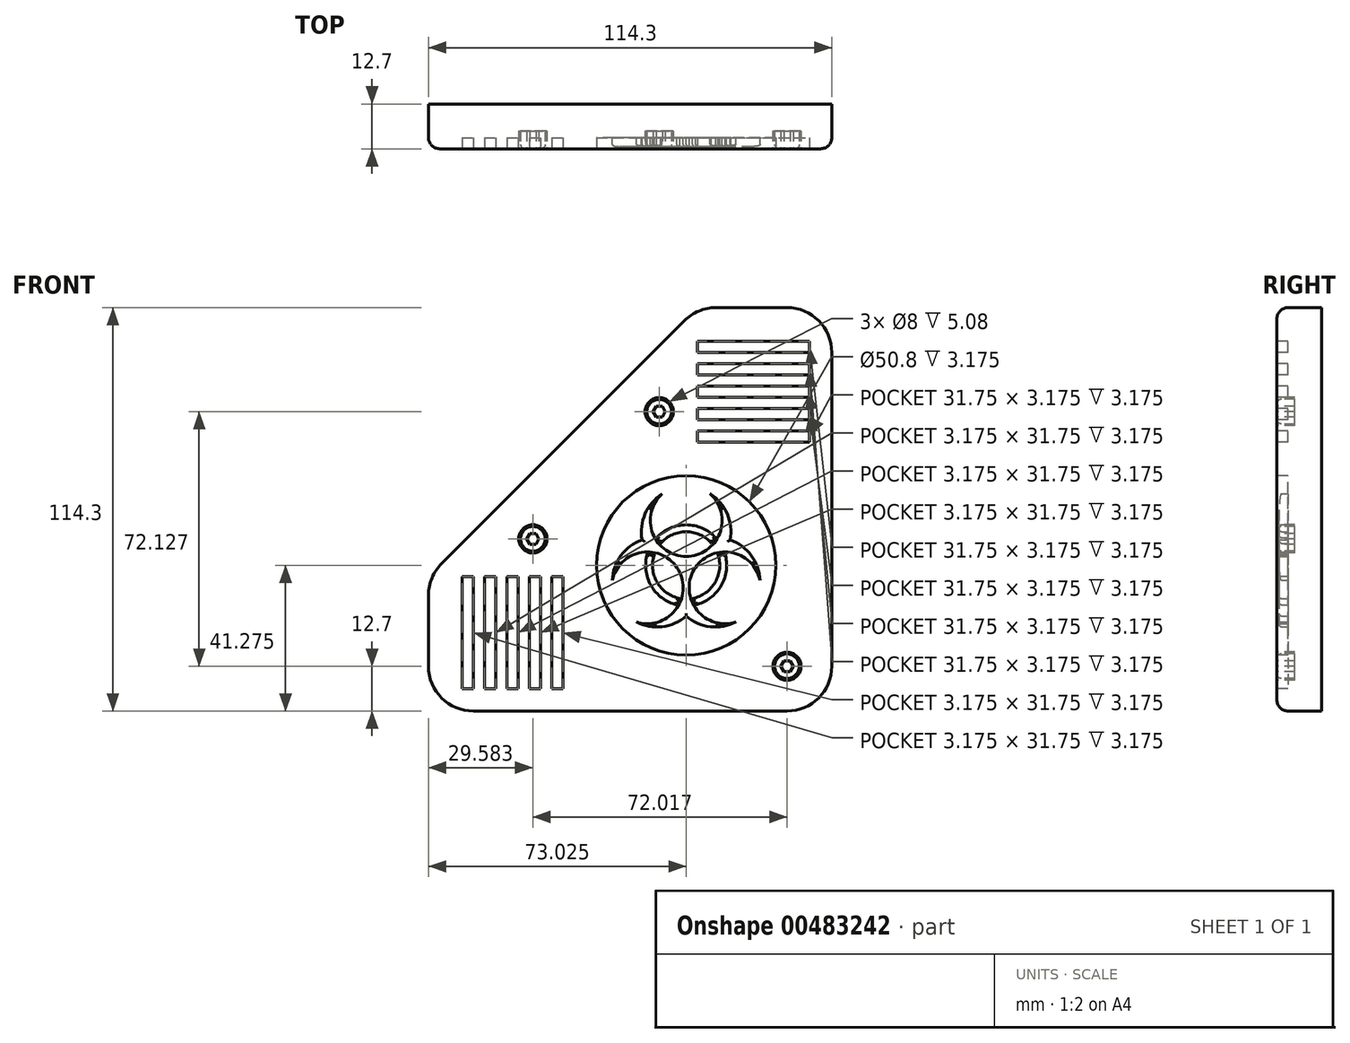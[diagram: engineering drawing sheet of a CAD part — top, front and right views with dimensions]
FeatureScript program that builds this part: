
annotation { "Feature Type Name" : "Feature", "Feature Type Description" : "" }
export const myFeature = defineFeature(function(context is Context, id is Id, definition is map)
    precondition{}
    {
        {
            var Q0;
            Q0=qCreatedBy(makeId("Front.planeOp"),FACE);
            var sketch = newSketch(context, id + "F0", { "sketchPlane" : qUnion([Q0])});
            skLineSegment(sketch, "E0.bottom", {"start": v(63.5, -76.2) * mm, "end": v(-25.4, -76.2) * mm});
            skLineSegment(sketch, "E0.left", {"start": v(76.2, -63.5) * mm, "end": v(76.2, 25.4) * mm});
            skPoint(sketch, "E0.middle", {"position": v(0, 0) * mm});
            skLineSegment(sketch, "E1", {"start": v(-34.38, -34.38) * mm, "end": v(34.38, 34.38) * mm});
            skPoint(sketch, "E0.right.end.orphan", {"position": v(-76.2, 76.2) * mm});
            skPoint(sketch, "E2.visualSharp", {"position": v(76.2, 76.2) * mm});
            skPoint(sketch, "E3.visualSharp", {"position": v(-76.2, -76.2) * mm});
            skPoint(sketch, "E4.visualSharp", {"position": v(76.2, -76.2) * mm});
            skArc(sketch, "E4.filletArc", {"start": v(63.5, -76.2) * mm, "mid": v(72.48, -72.48) * mm, "end": v(76.2, -63.5) * mm});
            skLineSegment(sketch, "E5", {"start": v(63.5, 38.1) * mm, "end": v(43.36, 38.1) * mm});
            skLineSegment(sketch, "E6", {"start": v(-38.1, -43.36) * mm, "end": v(-38.1, -63.5) * mm});
            skPoint(sketch, "E7.visualSharp", {"position": v(38.1, 38.1) * mm});
            skArc(sketch, "E7.filletArc", {"start": v(43.36, 38.1) * mm, "mid": v(38.5, 37.13) * mm, "end": v(34.38, 34.38) * mm});
            skPoint(sketch, "E8.visualSharp", {"position": v(76.2, 38.1) * mm});
            skArc(sketch, "E8.filletArc", {"start": v(76.2, 25.4) * mm, "mid": v(72.48, 34.38) * mm, "end": v(63.5, 38.1) * mm});
            skPoint(sketch, "E9.visualSharp", {"position": v(-38.1, -38.1) * mm});
            skArc(sketch, "E9.filletArc", {"start": v(-34.38, -34.38) * mm, "mid": v(-37.13, -38.5) * mm, "end": v(-38.1, -43.36) * mm});
            skPoint(sketch, "E10.visualSharp", {"position": v(-38.1, -76.2) * mm});
            skArc(sketch, "E10.filletArc", {"start": v(-38.1, -63.5) * mm, "mid": v(-34.38, -72.48) * mm, "end": v(-25.4, -76.2) * mm});
            skSolve(sketch);
        }
        {
            var Q0;
            Q0 = qSketchRegion(id + "F0", true);
            extrude(context, id + "F1", {"entities" : qUnion([Q0]), "depth" : 12.7 * mm});
        }
        {
            var Q0;
            Q0=makeQuery(id+"F1.opExtrude","CAP_FACE",FACE,{"disambiguationData":[OSD([sQuery(id+"F0.wireOp",EDGE,"E0.bottom"),sQuery(id+"F0.wireOp",EDGE,"E0.left"),sQuery(id+"F0.wireOp",EDGE,"E1"),sQuery(id+"F0.wireOp",EDGE,"E4.filletArc"),sQuery(id+"F0.wireOp",EDGE,"E5"),sQuery(id+"F0.wireOp",EDGE,"E6"),sQuery(id+"F0.wireOp",EDGE,"E7.filletArc"),sQuery(id+"F0.wireOp",EDGE,"E8.filletArc"),sQuery(id+"F0.wireOp",EDGE,"E9.filletArc"),sQuery(id+"F0.wireOp",EDGE,"E10.filletArc")])],"isStart":false});
            fillet(context, id + "F2", {"entities" : qUnion([Q0]), "radius" : 3.17 * mm, "tangentPropagation" : true, "allowEdgeOverflow" : false});
        }
        {
            var Q0;
            Q0=makeQuery(id+"F1.opExtrude","CAP_FACE",FACE,{"disambiguationData":[OSD([sQuery(id+"F0.wireOp",EDGE,"E0.bottom"),sQuery(id+"F0.wireOp",EDGE,"E0.left"),sQuery(id+"F0.wireOp",EDGE,"E1"),sQuery(id+"F0.wireOp",EDGE,"E4.filletArc"),sQuery(id+"F0.wireOp",EDGE,"E5"),sQuery(id+"F0.wireOp",EDGE,"E6"),sQuery(id+"F0.wireOp",EDGE,"E7.filletArc"),sQuery(id+"F0.wireOp",EDGE,"E8.filletArc"),sQuery(id+"F0.wireOp",EDGE,"E9.filletArc"),sQuery(id+"F0.wireOp",EDGE,"E10.filletArc")])],"isStart":false});
            var sketch = newSketch(context, id + "F3", { "sketchPlane" : qUnion([Q0])});
            skCircle(sketch, "E11", {"center": v(34.92, -34.92) * mm, "radius": 25.4 * mm});
            skSolve(sketch);
        }
        {
            var Q0;
            Q0 = qSketchRegion(id + "F3", true);
            extrude(context, id + "F4", {"entities" : qUnion([Q0]), "operationType" : NewBodyOperationType.REMOVE, "oppositeDirection" : true, "depth" : 3.17 * mm});
        }
        {
            var Q0;
            Q0=makeQuery(id+"F1.opExtrude","CAP_FACE",FACE,{"disambiguationData":[OSD([sQuery(id+"F0.wireOp",EDGE,"E0.bottom"),sQuery(id+"F0.wireOp",EDGE,"E0.left"),sQuery(id+"F0.wireOp",EDGE,"E1"),sQuery(id+"F0.wireOp",EDGE,"E4.filletArc"),sQuery(id+"F0.wireOp",EDGE,"E5"),sQuery(id+"F0.wireOp",EDGE,"E6"),sQuery(id+"F0.wireOp",EDGE,"E7.filletArc"),sQuery(id+"F0.wireOp",EDGE,"E8.filletArc"),sQuery(id+"F0.wireOp",EDGE,"E9.filletArc"),sQuery(id+"F0.wireOp",EDGE,"E10.filletArc")])],"isStart":false});
            var sketch = newSketch(context, id + "F5", { "sketchPlane" : qUnion([Q0])});
            skLineSegment(sketch, "E12.bottom", {"start": v(38.1, 0) * mm, "end": v(69.85, 0) * mm});
            skLineSegment(sketch, "E12.top", {"start": v(38.1, 3.18) * mm, "end": v(69.85, 3.18) * mm});
            skLineSegment(sketch, "E12.left", {"start": v(38.1, 0) * mm, "end": v(38.1, 3.18) * mm});
            skLineSegment(sketch, "E12.right", {"start": v(69.85, 0) * mm, "end": v(69.85, 3.18) * mm});
            skLineSegment(sketch, "E13.0.1.0", {"start": v(38.1, 9.53) * mm, "end": v(69.85, 9.53) * mm});
            skLineSegment(sketch, "E13.0.1.1", {"start": v(38.1, 6.35) * mm, "end": v(69.85, 6.35) * mm});
            skLineSegment(sketch, "E13.0.1.2", {"start": v(38.1, 6.35) * mm, "end": v(38.1, 9.53) * mm});
            skLineSegment(sketch, "E13.0.1.3", {"start": v(69.85, 6.35) * mm, "end": v(69.85, 9.53) * mm});
            skLineSegment(sketch, "E13.0.2.0", {"start": v(38.1, 15.88) * mm, "end": v(69.85, 15.88) * mm});
            skLineSegment(sketch, "E13.0.2.1", {"start": v(38.1, 12.7) * mm, "end": v(69.85, 12.7) * mm});
            skLineSegment(sketch, "E13.0.2.2", {"start": v(38.1, 12.7) * mm, "end": v(38.1, 15.88) * mm});
            skLineSegment(sketch, "E13.0.2.3", {"start": v(69.85, 12.7) * mm, "end": v(69.85, 15.88) * mm});
            skLineSegment(sketch, "E13.0.3.0", {"start": v(38.1, 22.23) * mm, "end": v(69.85, 22.23) * mm});
            skLineSegment(sketch, "E13.0.3.1", {"start": v(38.1, 19.05) * mm, "end": v(69.85, 19.05) * mm});
            skLineSegment(sketch, "E13.0.3.2", {"start": v(38.1, 19.05) * mm, "end": v(38.1, 22.23) * mm});
            skLineSegment(sketch, "E13.0.3.3", {"start": v(69.85, 19.05) * mm, "end": v(69.85, 22.23) * mm});
            skLineSegment(sketch, "E13.direction1", {"start": v(38.1, 0) * mm, "end": v(63.5, 0) * mm, "construction": true});
            skLineSegment(sketch, "E13.direction2", {"start": v(38.1, 0) * mm, "end": v(38.1, 6.35) * mm, "construction": true});
            skLineSegment(sketch, "E14.bottom", {"start": v(-3.17, -38.1) * mm, "end": v(0, -38.1) * mm});
            skLineSegment(sketch, "E14.top", {"start": v(-3.18, -69.85) * mm, "end": v(0, -69.85) * mm});
            skLineSegment(sketch, "E14.left", {"start": v(-3.17, -38.1) * mm, "end": v(-3.18, -69.85) * mm});
            skLineSegment(sketch, "E14.right", {"start": v(0, -38.1) * mm, "end": v(0, -69.85) * mm});
            skLineSegment(sketch, "E15.0.0.4", {"start": v(38.1, 28.58) * mm, "end": v(69.85, 28.58) * mm});
            skLineSegment(sketch, "E15.3.0.4", {"start": v(38.1, 25.4) * mm, "end": v(69.85, 25.4) * mm});
            skLineSegment(sketch, "E15.6.0.4", {"start": v(38.1, 25.4) * mm, "end": v(38.1, 28.58) * mm});
            skLineSegment(sketch, "E15.9.0.4", {"start": v(69.85, 25.4) * mm, "end": v(69.85, 28.58) * mm});
            skLineSegment(sketch, "E16.1.0.0", {"start": v(-6.35, -38.1) * mm, "end": v(-6.35, -69.85) * mm});
            skLineSegment(sketch, "E16.1.0.1", {"start": v(-9.52, -38.1) * mm, "end": v(-9.53, -69.85) * mm});
            skLineSegment(sketch, "E16.1.0.2", {"start": v(-9.53, -69.85) * mm, "end": v(-6.35, -69.85) * mm});
            skLineSegment(sketch, "E16.1.0.3", {"start": v(-9.52, -38.1) * mm, "end": v(-6.35, -38.1) * mm});
            skLineSegment(sketch, "E16.2.0.0", {"start": v(-12.7, -38.1) * mm, "end": v(-12.7, -69.85) * mm});
            skLineSegment(sketch, "E16.2.0.1", {"start": v(-15.87, -38.1) * mm, "end": v(-15.88, -69.85) * mm});
            skLineSegment(sketch, "E16.2.0.2", {"start": v(-15.88, -69.85) * mm, "end": v(-12.7, -69.85) * mm});
            skLineSegment(sketch, "E16.2.0.3", {"start": v(-15.87, -38.1) * mm, "end": v(-12.7, -38.1) * mm});
            skLineSegment(sketch, "E16.3.0.0", {"start": v(-19.05, -38.1) * mm, "end": v(-19.05, -69.85) * mm});
            skLineSegment(sketch, "E16.3.0.1", {"start": v(-22.22, -38.1) * mm, "end": v(-22.23, -69.85) * mm});
            skLineSegment(sketch, "E16.3.0.2", {"start": v(-22.23, -69.85) * mm, "end": v(-19.05, -69.85) * mm});
            skLineSegment(sketch, "E16.3.0.3", {"start": v(-22.22, -38.1) * mm, "end": v(-19.05, -38.1) * mm});
            skLineSegment(sketch, "E16.4.0.0", {"start": v(-25.4, -38.1) * mm, "end": v(-25.4, -69.85) * mm});
            skLineSegment(sketch, "E16.4.0.1", {"start": v(-28.57, -38.1) * mm, "end": v(-28.58, -69.85) * mm});
            skLineSegment(sketch, "E16.4.0.2", {"start": v(-28.58, -69.85) * mm, "end": v(-25.4, -69.85) * mm});
            skLineSegment(sketch, "E16.4.0.3", {"start": v(-28.57, -38.1) * mm, "end": v(-25.4, -38.1) * mm});
            skLineSegment(sketch, "E16.direction1", {"start": v(-3.18, -69.85) * mm, "end": v(-9.53, -69.85) * mm, "construction": true});
            skSolve(sketch);
        }
        {
            var Q0;
            Q0 = qSketchRegion(id + "F5", true);
            extrude(context, id + "F6", {"entities" : qUnion([Q0]), "operationType" : NewBodyOperationType.REMOVE, "oppositeDirection" : true, "depth" : 3.17 * mm});
        }
        {
            var Q0;
            Q0=makeQuery(id+"F4.boolean.opBoolean","COPY",FACE,{"derivedFrom":makeQuery(id+"F4.opExtrude","CAP_FACE",FACE,{"disambiguationData":[OSD([sQuery(id+"F3.wireOp",EDGE,"E11")])],"isStart":false})});
            var sketch = newSketch(context, id + "F7", { "sketchPlane" : qUnion([Q0])});
            skCircle(sketch, "E17.cCircle", {"center": v(34.92, -34.92) * mm, "radius": 25.4 * mm, "construction": true});
            skLineSegment(sketch, "E17.1", {"start": v(49.59, -9.52) * mm, "end": v(64.25, -34.92) * mm, "construction": true});
            skLineSegment(sketch, "E17.2", {"start": v(64.25, -34.92) * mm, "end": v(49.59, -60.32) * mm, "construction": true});
            skLineSegment(sketch, "E17.3", {"start": v(49.59, -60.32) * mm, "end": v(20.26, -60.32) * mm, "construction": true});
            skLineSegment(sketch, "E17.4", {"start": v(20.26, -60.32) * mm, "end": v(5.6, -34.92) * mm, "construction": true});
            skLineSegment(sketch, "E17.5", {"start": v(5.6, -34.92) * mm, "end": v(20.26, -9.52) * mm, "construction": true});
            skPoint(sketch, "E17.0.midPoint", {"position": v(34.92, -9.52) * mm});
            skLineSegment(sketch, "E18", {"start": v(34.92, -34.92) * mm, "end": v(56.92, -47.62) * mm, "construction": true});
            skLineSegment(sketch, "E19", {"start": v(34.92, -9.52) * mm, "end": v(34.92, -34.92) * mm, "construction": true});
            skLineSegment(sketch, "E20", {"start": v(34.92, -34.92) * mm, "end": v(12.93, -47.62) * mm, "construction": true});
            skArc(sketch, "E21", {"start": v(25.92, -31.83) * mm, "mid": v(26.68, -39.69) * mm, "end": v(33.1, -44.27) * mm});
            skArc(sketch, "E22", {"start": v(28.13, -14.67) * mm, "mid": v(23.29, -20.32) * mm, "end": v(22.44, -27.72) * mm});
            skArc(sketch, "E23", {"start": v(55.86, -39.17) * mm, "mid": v(53.4, -32.15) * mm, "end": v(47.41, -27.72) * mm});
            skArc(sketch, "E24", {"start": v(22.44, -27.72) * mm, "mid": v(16.46, -32.15) * mm, "end": v(13.99, -39.17) * mm});
            skCircle(sketch, "E25", {"center": v(34.92, -34.92) * mm, "radius": 12.7 * mm, "construction": true});
            skArc(sketch, "E26", {"start": v(28.13, -14.67) * mm, "mid": v(24.78, -21.72) * mm, "end": v(27.41, -29.07) * mm});
            skArc(sketch, "E27", {"start": v(20.78, -50.93) * mm, "mid": v(28.56, -50.32) * mm, "end": v(33.6, -44.36) * mm});
            skArc(sketch, "E28", {"start": v(55.86, -39.17) * mm, "mid": v(51.44, -32.74) * mm, "end": v(43.75, -31.35) * mm});
            skArc(sketch, "E29.trimOffspring", {"start": v(20.78, -50.93) * mm, "mid": v(28.1, -52.3) * mm, "end": v(34.92, -49.34) * mm});
            skArc(sketch, "E30.trimOffspring", {"start": v(34.92, -49.34) * mm, "mid": v(41.75, -52.3) * mm, "end": v(49.07, -50.93) * mm});
            skArc(sketch, "E31.trimOffspring", {"start": v(47.41, -27.72) * mm, "mid": v(46.56, -20.32) * mm, "end": v(41.72, -14.67) * mm});
            skArc(sketch, "E32", {"start": v(23.93, -31.62) * mm, "mid": v(24.98, -40.67) * mm, "end": v(32.29, -46.1) * mm});
            skArc(sketch, "E33.trimOffspring", {"start": v(27.41, -29.07) * mm, "mid": v(34.92, -32.38) * mm, "end": v(42.44, -29.07) * mm});
            skArc(sketch, "E34.trimOffspring", {"start": v(26.1, -31.35) * mm, "mid": v(18.41, -32.74) * mm, "end": v(13.99, -39.17) * mm});
            skArc(sketch, "E35.trimOffspring", {"start": v(42.1, -28.67) * mm, "mid": v(34.92, -25.4) * mm, "end": v(27.74, -28.67) * mm});
            skArc(sketch, "E36.trimOffspring", {"start": v(43.28, -27.05) * mm, "mid": v(34.92, -23.44) * mm, "end": v(26.57, -27.05) * mm});
            skArc(sketch, "E37.trimOffspring", {"start": v(42.44, -29.07) * mm, "mid": v(45.07, -21.72) * mm, "end": v(41.72, -14.67) * mm});
            skArc(sketch, "E38.trimOffspring", {"start": v(43.75, -31.35) * mm, "mid": v(37.12, -36.2) * mm, "end": v(36.24, -44.36) * mm});
            skArc(sketch, "E39.trimOffspring", {"start": v(36.75, -44.27) * mm, "mid": v(43.17, -39.69) * mm, "end": v(43.93, -31.83) * mm});
            skArc(sketch, "E40.trimOffspring", {"start": v(37.56, -46.1) * mm, "mid": v(44.87, -40.67) * mm, "end": v(45.92, -31.62) * mm});
            skArc(sketch, "E41.trimOffspring", {"start": v(33.6, -44.36) * mm, "mid": v(32.73, -36.2) * mm, "end": v(26.1, -31.35) * mm});
            skArc(sketch, "E42.trimOffspring", {"start": v(36.24, -44.36) * mm, "mid": v(41.29, -50.32) * mm, "end": v(49.07, -50.93) * mm});
            skLineSegment(sketch, "E43", {"start": v(34.92, -34.92) * mm, "end": v(12.93, -22.22) * mm, "construction": true});
            skLineSegment(sketch, "E44", {"start": v(34.92, -34.92) * mm, "end": v(56.92, -22.22) * mm, "construction": true});
            skLineSegment(sketch, "E45", {"start": v(34.92, -34.92) * mm, "end": v(34.92, -60.32) * mm, "construction": true});
            skArc(sketch, "E46", {"start": v(26.57, -27.05) * mm, "mid": v(27.11, -27.9) * mm, "end": v(27.74, -28.67) * mm});
            skArc(sketch, "E47", {"start": v(43.28, -27.05) * mm, "mid": v(42.74, -27.9) * mm, "end": v(42.1, -28.67) * mm});
            skArc(sketch, "E48", {"start": v(23.93, -31.62) * mm, "mid": v(24.93, -31.67) * mm, "end": v(25.92, -31.83) * mm});
            skArc(sketch, "E49", {"start": v(32.29, -46.1) * mm, "mid": v(32.74, -45.2) * mm, "end": v(33.1, -44.27) * mm});
            skArc(sketch, "E50", {"start": v(37.56, -46.1) * mm, "mid": v(37.1, -45.2) * mm, "end": v(36.75, -44.27) * mm});
            skArc(sketch, "E51", {"start": v(45.92, -31.62) * mm, "mid": v(44.92, -31.67) * mm, "end": v(43.93, -31.83) * mm});
            skSolve(sketch);
        }
        {
            var Q0;
            Q0 = qSketchRegion(id + "F7", true);
            extrude(context, id + "F8", {"entities" : qUnion([Q0]), "operationType" : NewBodyOperationType.ADD, "depth" : 2.54 * mm});
        }
        {
            var Q0;
            Q0=makeQuery(id+"F8.opExtrude","CAP_FACE",FACE,{"disambiguationData":[OSD([sQuery(id+"F7.wireOp",EDGE,"E22"),sQuery(id+"F7.wireOp",EDGE,"E23"),sQuery(id+"F7.wireOp",EDGE,"E24"),sQuery(id+"F7.wireOp",EDGE,"E26"),sQuery(id+"F7.wireOp",EDGE,"E27"),sQuery(id+"F7.wireOp",EDGE,"E28"),sQuery(id+"F7.wireOp",EDGE,"E29.trimOffspring"),sQuery(id+"F7.wireOp",EDGE,"E30.trimOffspring"),sQuery(id+"F7.wireOp",EDGE,"E31.trimOffspring"),sQuery(id+"F7.wireOp",EDGE,"E33.trimOffspring"),sQuery(id+"F7.wireOp",EDGE,"E34.trimOffspring"),sQuery(id+"F7.wireOp",EDGE,"E37.trimOffspring"),sQuery(id+"F7.wireOp",EDGE,"E38.trimOffspring"),sQuery(id+"F7.wireOp",EDGE,"E41.trimOffspring"),sQuery(id+"F7.wireOp",EDGE,"E42.trimOffspring")])],"isStart":false});
            var Q1;
            Q1=makeQuery(id+"F8.opExtrude","CAP_FACE",FACE,{"disambiguationData":[OSD([sQuery(id+"F7.wireOp",EDGE,"E21"),sQuery(id+"F7.wireOp",EDGE,"E32"),sQuery(id+"F7.wireOp",EDGE,"E48"),sQuery(id+"F7.wireOp",EDGE,"E49")])],"isStart":false});
            var Q2;
            Q2=makeQuery(id+"F8.opExtrude","CAP_FACE",FACE,{"disambiguationData":[OSD([sQuery(id+"F7.wireOp",EDGE,"E35.trimOffspring"),sQuery(id+"F7.wireOp",EDGE,"E36.trimOffspring"),sQuery(id+"F7.wireOp",EDGE,"E46"),sQuery(id+"F7.wireOp",EDGE,"E47")])],"isStart":false});
            var Q3;
            Q3=makeQuery(id+"F8.opExtrude","CAP_FACE",FACE,{"disambiguationData":[OSD([sQuery(id+"F7.wireOp",EDGE,"E39.trimOffspring"),sQuery(id+"F7.wireOp",EDGE,"E40.trimOffspring"),sQuery(id+"F7.wireOp",EDGE,"E50"),sQuery(id+"F7.wireOp",EDGE,"E51")])],"isStart":false});
            fillet(context, id + "F9", {"entities" : qUnion([Q0, Q1, Q2, Q3]), "radius" : 0.64 * mm, "tangentPropagation" : true, "allowEdgeOverflow" : false});
        }
        {
            var Q0;
            Q0=makeQuery(id+"F1.opExtrude","CAP_FACE",FACE,{"disambiguationData":[OSD([sQuery(id+"F0.wireOp",EDGE,"E0.bottom"),sQuery(id+"F0.wireOp",EDGE,"E0.left"),sQuery(id+"F0.wireOp",EDGE,"E1"),sQuery(id+"F0.wireOp",EDGE,"E4.filletArc"),sQuery(id+"F0.wireOp",EDGE,"E5"),sQuery(id+"F0.wireOp",EDGE,"E6"),sQuery(id+"F0.wireOp",EDGE,"E7.filletArc"),sQuery(id+"F0.wireOp",EDGE,"E8.filletArc"),sQuery(id+"F0.wireOp",EDGE,"E9.filletArc"),sQuery(id+"F0.wireOp",EDGE,"E10.filletArc")])],"isStart":false});
            var sketch = newSketch(context, id + "F10", { "sketchPlane" : qUnion([Q0])});
            skLineSegment(sketch, "E52", {"start": v(0, 0) * mm, "end": v(70.24, -70.24) * mm, "construction": true});
            skLineSegment(sketch, "E53", {"start": v(-34.92, -53.97) * mm, "end": v(53.43, 34.93) * mm, "construction": true});
            skPoint(sketch, "E53.startSnap0", {"position": v(-28.58, -53.97) * mm});
            skCircle(sketch, "E54", {"center": v(63.5, -63.5) * mm, "radius": 4 * mm});
            skCircle(sketch, "E55", {"center": v(-8.52, -27.4) * mm, "radius": 4 * mm});
            skCircle(sketch, "E56", {"center": v(27.3, 8.63) * mm, "radius": 4 * mm});
            skCircle(sketch, "E57", {"center": v(27.3, 8.63) * mm, "radius": 3.5 * mm});
            skCircle(sketch, "E58", {"center": v(-8.52, -27.4) * mm, "radius": 3.5 * mm});
            skCircle(sketch, "E59", {"center": v(63.5, -63.5) * mm, "radius": 3.5 * mm});
            skSolve(sketch);
        }
        {
            var Q0;
            Q0 = qSketchRegion(id + "F10", true);
            extrude(context, id + "F11", {"entities" : qUnion([Q0]), "operationType" : NewBodyOperationType.REMOVE, "oppositeDirection" : true, "depth" : 5.08 * mm});
        }
        {
            var Q0;
            {var subQ0=sQuery(id+"F0.wireOp",EDGE,"E10.filletArc");var subQ1=sQuery(id+"F0.wireOp",EDGE,"E9.filletArc");var subQ2=sQuery(id+"F0.wireOp",EDGE,"E8.filletArc");var subQ3=sQuery(id+"F0.wireOp",EDGE,"E6");var subQ4=sQuery(id+"F0.wireOp",EDGE,"E5");var subQ5=sQuery(id+"F0.wireOp",EDGE,"E0.bottom");var subQ6=sQuery(id+"F0.wireOp",EDGE,"E0.left");var subQ7=sQuery(id+"F0.wireOp",EDGE,"E1");var subQ8=sQuery(id+"F0.wireOp",EDGE,"E4.filletArc");var subQ9=sQuery(id+"F0.wireOp",EDGE,"E7.filletArc");Q0=makeQuery(id+"F11.boolean.opBoolean","SPLIT",FACE,{"disambiguationData":[TD([makeQuery(id+"F2.opFillet","BLEND_FACE",FACE,{"disambiguationData":[OSD([subQ5])]})])],"derivedFrom":makeQuery(id+"F1.opExtrude","CAP_FACE",FACE,{"disambiguationData":[OSD([subQ5,subQ6,subQ7,subQ8,subQ4,subQ3,subQ9,subQ2,subQ1,subQ0])],"isStart":false})});}
            var sketch = newSketch(context, id + "F12", { "sketchPlane" : qUnion([Q0])});
            skCircle(sketch, "E60.cCircle", {"center": v(27.3, 8.63) * mm, "radius": 1.5 * mm, "construction": true});
            skLineSegment(sketch, "E60.0", {"start": v(26.43, 10.13) * mm, "end": v(28.16, 10.13) * mm});
            skLineSegment(sketch, "E60.1", {"start": v(28.16, 10.13) * mm, "end": v(29.03, 8.63) * mm});
            skLineSegment(sketch, "E60.2", {"start": v(29.03, 8.63) * mm, "end": v(28.16, 7.13) * mm});
            skLineSegment(sketch, "E60.3", {"start": v(28.16, 7.13) * mm, "end": v(26.43, 7.13) * mm});
            skLineSegment(sketch, "E60.4", {"start": v(26.43, 7.13) * mm, "end": v(25.56, 8.63) * mm});
            skLineSegment(sketch, "E60.5", {"start": v(25.56, 8.63) * mm, "end": v(26.43, 10.13) * mm});
            skPoint(sketch, "E60.0.midPoint", {"position": v(27.3, 10.13) * mm});
            skCircle(sketch, "E61.cCircle", {"center": v(-8.52, -27.4) * mm, "radius": 1.5 * mm, "construction": true});
            skLineSegment(sketch, "E61.0", {"start": v(-9.38, -25.9) * mm, "end": v(-7.65, -25.9) * mm});
            skLineSegment(sketch, "E61.1", {"start": v(-7.65, -25.9) * mm, "end": v(-6.78, -27.4) * mm});
            skLineSegment(sketch, "E61.2", {"start": v(-6.78, -27.4) * mm, "end": v(-7.65, -28.9) * mm});
            skLineSegment(sketch, "E61.3", {"start": v(-7.65, -28.9) * mm, "end": v(-9.38, -28.9) * mm});
            skLineSegment(sketch, "E61.4", {"start": v(-9.38, -28.9) * mm, "end": v(-10.25, -27.4) * mm});
            skLineSegment(sketch, "E61.5", {"start": v(-10.25, -27.4) * mm, "end": v(-9.38, -25.9) * mm});
            skPoint(sketch, "E61.0.midPoint", {"position": v(-8.52, -25.9) * mm});
            skCircle(sketch, "E62.cCircle", {"center": v(63.5, -63.5) * mm, "radius": 1.5 * mm, "construction": true});
            skLineSegment(sketch, "E62.0", {"start": v(62.63, -62) * mm, "end": v(64.37, -62) * mm});
            skLineSegment(sketch, "E62.1", {"start": v(64.37, -62) * mm, "end": v(65.23, -63.5) * mm});
            skLineSegment(sketch, "E62.2", {"start": v(65.23, -63.5) * mm, "end": v(64.37, -65) * mm});
            skLineSegment(sketch, "E62.3", {"start": v(64.37, -65) * mm, "end": v(62.63, -65) * mm});
            skLineSegment(sketch, "E62.4", {"start": v(62.63, -65) * mm, "end": v(61.77, -63.5) * mm});
            skLineSegment(sketch, "E62.5", {"start": v(61.77, -63.5) * mm, "end": v(62.63, -62) * mm});
            skPoint(sketch, "E62.0.midPoint", {"position": v(63.5, -62) * mm});
            skSolve(sketch);
        }
        {
            var Q0;
            Q0 = qSketchRegion(id + "F12", true);
            extrude(context, id + "F13", {"entities" : qUnion([Q0]), "operationType" : NewBodyOperationType.REMOVE, "oppositeDirection" : true, "depth" : 5.08 * mm});
        }
        {
            var Q0;
            Q0=makeQuery(id+"F11.boolean.opBoolean","COPY",EDGE,{"derivedFrom":makeQuery(id+"F11.opExtrude","CAP_EDGE",EDGE,{"disambiguationData":[OSD([sQuery(id+"F10.wireOp",EDGE,"E58")])],"isStart":true})});
            var Q1;
            Q1=makeQuery(id+"F11.boolean.opBoolean","COPY",EDGE,{"derivedFrom":makeQuery(id+"F11.opExtrude","CAP_EDGE",EDGE,{"disambiguationData":[OSD([sQuery(id+"F10.wireOp",EDGE,"E59")])],"isStart":true})});
            var Q2;
            Q2=makeQuery(id+"F11.boolean.opBoolean","COPY",EDGE,{"derivedFrom":makeQuery(id+"F11.opExtrude","CAP_EDGE",EDGE,{"disambiguationData":[OSD([sQuery(id+"F10.wireOp",EDGE,"E57")])],"isStart":true})});
            var Q3;
            Q3=makeQuery(id+"F6.boolean.opBoolean","COPY",EDGE,{"derivedFrom":makeQuery(id+"F6.opExtrude","CAP_EDGE",EDGE,{"disambiguationData":[OSD([sQuery(id+"F5.wireOp",EDGE,"E15.6.0.4")])],"isStart":true})});
            var Q4;
            Q4=makeQuery(id+"F6.boolean.opBoolean","COPY",EDGE,{"derivedFrom":makeQuery(id+"F6.opExtrude","CAP_EDGE",EDGE,{"disambiguationData":[OSD([sQuery(id+"F5.wireOp",EDGE,"E13.0.3.2")])],"isStart":true})});
            var Q5;
            Q5=makeQuery(id+"F6.boolean.opBoolean","COPY",EDGE,{"derivedFrom":makeQuery(id+"F6.opExtrude","CAP_EDGE",EDGE,{"disambiguationData":[OSD([sQuery(id+"F5.wireOp",EDGE,"E13.0.2.2")])],"isStart":true})});
            var Q6;
            Q6=makeQuery(id+"F6.boolean.opBoolean","COPY",EDGE,{"derivedFrom":makeQuery(id+"F6.opExtrude","CAP_EDGE",EDGE,{"disambiguationData":[OSD([sQuery(id+"F5.wireOp",EDGE,"E13.0.1.2")])],"isStart":true})});
            var Q7;
            Q7=makeQuery(id+"F6.boolean.opBoolean","COPY",EDGE,{"derivedFrom":makeQuery(id+"F6.opExtrude","CAP_EDGE",EDGE,{"disambiguationData":[OSD([sQuery(id+"F5.wireOp",EDGE,"E12.left")])],"isStart":true})});
            var Q8;
            Q8=makeQuery(id+"F6.boolean.opBoolean","COPY",EDGE,{"derivedFrom":makeQuery(id+"F6.opExtrude","CAP_EDGE",EDGE,{"disambiguationData":[OSD([sQuery(id+"F5.wireOp",EDGE,"E12.right")])],"isStart":true})});
            var Q9;
            Q9=makeQuery(id+"F6.boolean.opBoolean","COPY",EDGE,{"derivedFrom":makeQuery(id+"F6.opExtrude","CAP_EDGE",EDGE,{"disambiguationData":[OSD([sQuery(id+"F5.wireOp",EDGE,"E13.0.1.3")])],"isStart":true})});
            var Q10;
            Q10=makeQuery(id+"F6.boolean.opBoolean","COPY",EDGE,{"derivedFrom":makeQuery(id+"F6.opExtrude","CAP_EDGE",EDGE,{"disambiguationData":[OSD([sQuery(id+"F5.wireOp",EDGE,"E13.0.2.3")])],"isStart":true})});
            var Q11;
            Q11=makeQuery(id+"F6.boolean.opBoolean","COPY",EDGE,{"derivedFrom":makeQuery(id+"F6.opExtrude","CAP_EDGE",EDGE,{"disambiguationData":[OSD([sQuery(id+"F5.wireOp",EDGE,"E13.0.3.3")])],"isStart":true})});
            var Q12;
            Q12=makeQuery(id+"F6.boolean.opBoolean","COPY",EDGE,{"derivedFrom":makeQuery(id+"F6.opExtrude","CAP_EDGE",EDGE,{"disambiguationData":[OSD([sQuery(id+"F5.wireOp",EDGE,"E15.9.0.4")])],"isStart":true})});
            var Q13;
            Q13=makeQuery(id+"F6.boolean.opBoolean","COPY",EDGE,{"derivedFrom":makeQuery(id+"F6.opExtrude","CAP_EDGE",EDGE,{"disambiguationData":[OSD([sQuery(id+"F5.wireOp",EDGE,"E15.0.0.4")])],"isStart":true})});
            var Q14;
            Q14=makeQuery(id+"F6.boolean.opBoolean","COPY",EDGE,{"derivedFrom":makeQuery(id+"F6.opExtrude","CAP_EDGE",EDGE,{"disambiguationData":[OSD([sQuery(id+"F5.wireOp",EDGE,"E15.3.0.4")])],"isStart":true})});
            var Q15;
            Q15=makeQuery(id+"F6.boolean.opBoolean","COPY",EDGE,{"derivedFrom":makeQuery(id+"F6.opExtrude","CAP_EDGE",EDGE,{"disambiguationData":[OSD([sQuery(id+"F5.wireOp",EDGE,"E13.0.3.0")])],"isStart":true})});
            var Q16;
            Q16=makeQuery(id+"F6.boolean.opBoolean","COPY",EDGE,{"derivedFrom":makeQuery(id+"F6.opExtrude","CAP_EDGE",EDGE,{"disambiguationData":[OSD([sQuery(id+"F5.wireOp",EDGE,"E13.0.3.1")])],"isStart":true})});
            var Q17;
            Q17=makeQuery(id+"F6.boolean.opBoolean","COPY",EDGE,{"derivedFrom":makeQuery(id+"F6.opExtrude","CAP_EDGE",EDGE,{"disambiguationData":[OSD([sQuery(id+"F5.wireOp",EDGE,"E13.0.2.0")])],"isStart":true})});
            var Q18;
            Q18=makeQuery(id+"F6.boolean.opBoolean","COPY",EDGE,{"derivedFrom":makeQuery(id+"F6.opExtrude","CAP_EDGE",EDGE,{"disambiguationData":[OSD([sQuery(id+"F5.wireOp",EDGE,"E13.0.2.1")])],"isStart":true})});
            var Q19;
            Q19=makeQuery(id+"F6.boolean.opBoolean","COPY",EDGE,{"derivedFrom":makeQuery(id+"F6.opExtrude","CAP_EDGE",EDGE,{"disambiguationData":[OSD([sQuery(id+"F5.wireOp",EDGE,"E13.0.1.0")])],"isStart":true})});
            var Q20;
            Q20=makeQuery(id+"F6.boolean.opBoolean","COPY",EDGE,{"derivedFrom":makeQuery(id+"F6.opExtrude","CAP_EDGE",EDGE,{"disambiguationData":[OSD([sQuery(id+"F5.wireOp",EDGE,"E13.0.1.1")])],"isStart":true})});
            var Q21;
            Q21=makeQuery(id+"F6.boolean.opBoolean","COPY",EDGE,{"derivedFrom":makeQuery(id+"F6.opExtrude","CAP_EDGE",EDGE,{"disambiguationData":[OSD([sQuery(id+"F5.wireOp",EDGE,"E12.top")])],"isStart":true})});
            var Q22;
            Q22=makeQuery(id+"F6.boolean.opBoolean","COPY",EDGE,{"derivedFrom":makeQuery(id+"F6.opExtrude","CAP_EDGE",EDGE,{"disambiguationData":[OSD([sQuery(id+"F5.wireOp",EDGE,"E12.bottom")])],"isStart":true})});
            var Q23;
            Q23=makeQuery(id+"F6.boolean.opBoolean","COPY",EDGE,{"derivedFrom":makeQuery(id+"F6.opExtrude","CAP_EDGE",EDGE,{"disambiguationData":[OSD([sQuery(id+"F5.wireOp",EDGE,"E16.4.0.3")])],"isStart":true})});
            var Q24;
            Q24=makeQuery(id+"F6.boolean.opBoolean","COPY",EDGE,{"derivedFrom":makeQuery(id+"F6.opExtrude","CAP_EDGE",EDGE,{"disambiguationData":[OSD([sQuery(id+"F5.wireOp",EDGE,"E16.2.0.3")])],"isStart":true})});
            var Q25;
            Q25=makeQuery(id+"F6.boolean.opBoolean","COPY",EDGE,{"derivedFrom":makeQuery(id+"F6.opExtrude","CAP_EDGE",EDGE,{"disambiguationData":[OSD([sQuery(id+"F5.wireOp",EDGE,"E16.1.0.3")])],"isStart":true})});
            var Q26;
            Q26=makeQuery(id+"F6.boolean.opBoolean","COPY",EDGE,{"derivedFrom":makeQuery(id+"F6.opExtrude","CAP_EDGE",EDGE,{"disambiguationData":[OSD([sQuery(id+"F5.wireOp",EDGE,"E14.bottom")])],"isStart":true})});
            var Q27;
            Q27=makeQuery(id+"F6.boolean.opBoolean","COPY",EDGE,{"derivedFrom":makeQuery(id+"F6.opExtrude","CAP_EDGE",EDGE,{"disambiguationData":[OSD([sQuery(id+"F5.wireOp",EDGE,"E16.4.0.2")])],"isStart":true})});
            var Q28;
            Q28=makeQuery(id+"F6.boolean.opBoolean","COPY",EDGE,{"derivedFrom":makeQuery(id+"F6.opExtrude","CAP_EDGE",EDGE,{"disambiguationData":[OSD([sQuery(id+"F5.wireOp",EDGE,"E16.3.0.2")])],"isStart":true})});
            var Q29;
            Q29=makeQuery(id+"F6.boolean.opBoolean","COPY",EDGE,{"derivedFrom":makeQuery(id+"F6.opExtrude","CAP_EDGE",EDGE,{"disambiguationData":[OSD([sQuery(id+"F5.wireOp",EDGE,"E16.2.0.2")])],"isStart":true})});
            var Q30;
            Q30=makeQuery(id+"F6.boolean.opBoolean","COPY",EDGE,{"derivedFrom":makeQuery(id+"F6.opExtrude","CAP_EDGE",EDGE,{"disambiguationData":[OSD([sQuery(id+"F5.wireOp",EDGE,"E16.1.0.2")])],"isStart":true})});
            var Q31;
            Q31=makeQuery(id+"F6.boolean.opBoolean","COPY",EDGE,{"derivedFrom":makeQuery(id+"F6.opExtrude","CAP_EDGE",EDGE,{"disambiguationData":[OSD([sQuery(id+"F5.wireOp",EDGE,"E14.top")])],"isStart":true})});
            var Q32;
            Q32=makeQuery(id+"F6.boolean.opBoolean","COPY",EDGE,{"derivedFrom":makeQuery(id+"F6.opExtrude","CAP_EDGE",EDGE,{"disambiguationData":[OSD([sQuery(id+"F5.wireOp",EDGE,"E16.4.0.1")])],"isStart":true})});
            var Q33;
            Q33=makeQuery(id+"F6.boolean.opBoolean","COPY",EDGE,{"derivedFrom":makeQuery(id+"F6.opExtrude","CAP_EDGE",EDGE,{"disambiguationData":[OSD([sQuery(id+"F5.wireOp",EDGE,"E16.4.0.0")])],"isStart":true})});
            var Q34;
            Q34=makeQuery(id+"F6.boolean.opBoolean","COPY",EDGE,{"derivedFrom":makeQuery(id+"F6.opExtrude","CAP_EDGE",EDGE,{"disambiguationData":[OSD([sQuery(id+"F5.wireOp",EDGE,"E16.3.0.1")])],"isStart":true})});
            var Q35;
            Q35=makeQuery(id+"F6.boolean.opBoolean","COPY",EDGE,{"derivedFrom":makeQuery(id+"F6.opExtrude","CAP_EDGE",EDGE,{"disambiguationData":[OSD([sQuery(id+"F5.wireOp",EDGE,"E16.3.0.0")])],"isStart":true})});
            var Q36;
            Q36=makeQuery(id+"F6.boolean.opBoolean","COPY",EDGE,{"derivedFrom":makeQuery(id+"F6.opExtrude","CAP_EDGE",EDGE,{"disambiguationData":[OSD([sQuery(id+"F5.wireOp",EDGE,"E16.2.0.1")])],"isStart":true})});
            var Q37;
            Q37=makeQuery(id+"F6.boolean.opBoolean","COPY",EDGE,{"derivedFrom":makeQuery(id+"F6.opExtrude","CAP_EDGE",EDGE,{"disambiguationData":[OSD([sQuery(id+"F5.wireOp",EDGE,"E16.2.0.0")])],"isStart":true})});
            var Q38;
            Q38=makeQuery(id+"F6.boolean.opBoolean","COPY",EDGE,{"derivedFrom":makeQuery(id+"F6.opExtrude","CAP_EDGE",EDGE,{"disambiguationData":[OSD([sQuery(id+"F5.wireOp",EDGE,"E16.3.0.3")])],"isStart":true})});
            var Q39;
            Q39=makeQuery(id+"F6.boolean.opBoolean","COPY",EDGE,{"derivedFrom":makeQuery(id+"F6.opExtrude","CAP_EDGE",EDGE,{"disambiguationData":[OSD([sQuery(id+"F5.wireOp",EDGE,"E16.1.0.1")])],"isStart":true})});
            var Q40;
            Q40=makeQuery(id+"F6.boolean.opBoolean","COPY",EDGE,{"derivedFrom":makeQuery(id+"F6.opExtrude","CAP_EDGE",EDGE,{"disambiguationData":[OSD([sQuery(id+"F5.wireOp",EDGE,"E16.1.0.0")])],"isStart":true})});
            var Q41;
            Q41=makeQuery(id+"F6.boolean.opBoolean","COPY",EDGE,{"derivedFrom":makeQuery(id+"F6.opExtrude","CAP_EDGE",EDGE,{"disambiguationData":[OSD([sQuery(id+"F5.wireOp",EDGE,"E14.left")])],"isStart":true})});
            var Q42;
            Q42=makeQuery(id+"F6.boolean.opBoolean","COPY",EDGE,{"derivedFrom":makeQuery(id+"F6.opExtrude","CAP_EDGE",EDGE,{"disambiguationData":[OSD([sQuery(id+"F5.wireOp",EDGE,"E14.right")])],"isStart":true})});
            fillet(context, id + "F14", {"entities" : qUnion([Q0, Q1, Q2, Q3, Q4, Q5, Q6, Q7, Q8, Q9, Q10, Q11, Q12, Q13, Q14, Q15, Q16, Q17, Q18, Q19, Q20, Q21, Q22, Q23, Q24, Q25, Q26, Q27, Q28, Q29, Q30, Q31, Q32, Q33, Q34, Q35, Q36, Q37, Q38, Q39, Q40, Q41, Q42]), "radius" : 1.27 * mm, "tangentPropagation" : true, "allowEdgeOverflow" : false});
        }
    });
